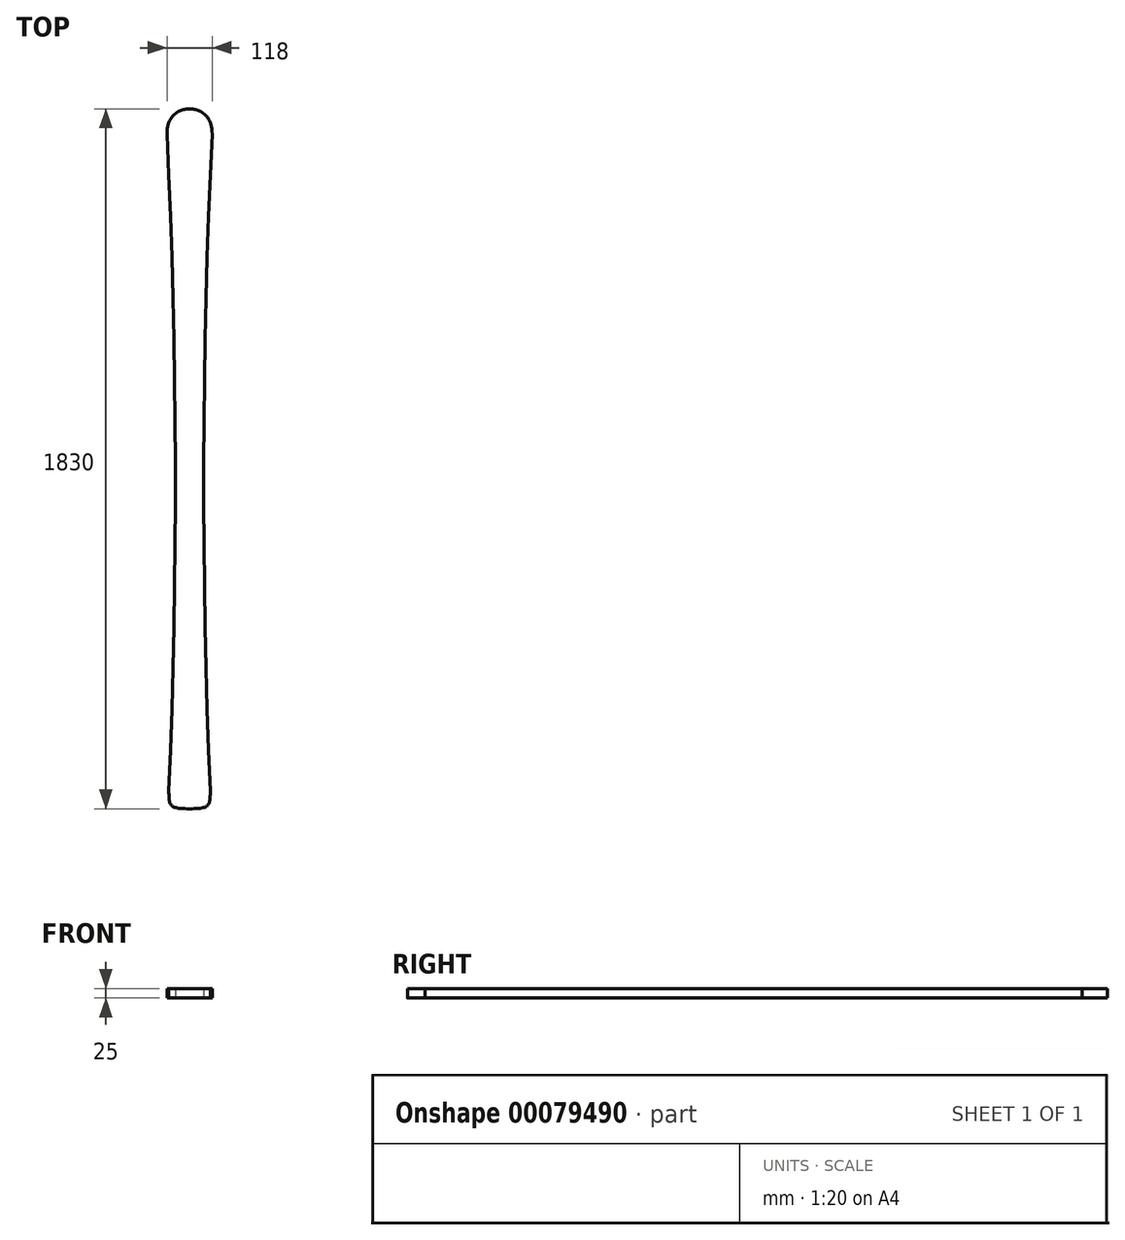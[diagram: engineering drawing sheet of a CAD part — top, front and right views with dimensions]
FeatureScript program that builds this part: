
annotation { "Feature Type Name" : "Feature", "Feature Type Description" : "" }
export const myFeature = defineFeature(function(context is Context, id is Id, definition is map)
    precondition{}
    {
        {
            var Q0;
            Q0=qCreatedBy(makeId("Top.planeOp"),FACE);
            var sketch = newSketch(context, id + "F0", { "sketchPlane" : qUnion([Q0])});
            skLineSegment(sketch, "E0", {"start": v(0, 0) * mm, "end": v(0, 1830) * mm, "construction": true});
            skLineSegment(sketch, "E1", {"start": v(0, 1830) * mm, "end": v(59, 1830) * mm, "construction": true});
            skLineSegment(sketch, "E2", {"start": v(59, 1830) * mm, "end": v(59, 0) * mm, "construction": true});
            skLineSegment(sketch, "E3", {"start": v(54, 0) * mm, "end": v(54, 46.44) * mm, "construction": true});
            skLineSegment(sketch, "E4", {"start": v(0, 1764.07) * mm, "end": v(59, 1764.07) * mm, "construction": true});
            skLineSegment(sketch, "E5", {"start": v(0, 46.44) * mm, "end": v(54, 46.44) * mm, "construction": true});
            skLineSegment(sketch, "E6", {"start": v(37, 1094.84) * mm, "end": v(37, 850) * mm, "construction": true});
            skArc(sketch, "E7", {"start": v(59, 1764.07) * mm, "mid": v(37.08, 905.3) * mm, "end": v(54, 46.44) * mm});
            skFitSpline(sketch, "E8", {"points": [v(59, 1764.07) * mm, v(0, 1830) * mm], "startDerivative": vector(0, 163.98) * mm, "endDerivative": vector(-63.63, 0) * mm});
            skFitSpline(sketch, "E9", {"points": [v(54, 46.44) * mm, v(0, 0) * mm], "startDerivative": vector(0, -114.92) * mm, "endDerivative": vector(-161.21, 0) * mm});
            skFitSpline(sketch, "E10.MirrorCS", {"points": [v(-59, 1764.07) * mm, v(0, 1830) * mm], "startDerivative": vector(0, 163.98) * mm, "endDerivative": vector(63.63, 0) * mm});
            skArc(sketch, "E11.MirrorCS", {"start": v(-59, 1764.07) * mm, "mid": v(-37.08, 905.3) * mm, "end": v(-54, 46.44) * mm});
            skFitSpline(sketch, "E12.MirrorCS", {"points": [v(-54, 46.44) * mm, v(0, 0) * mm], "startDerivative": vector(0, -114.92) * mm, "endDerivative": vector(161.21, 0) * mm});
            skPoint(sketch, "E13", {"position": v(37, 850) * mm});
            skSolve(sketch);
        }
        {
            var Q0;
            Q0=makeQuery(id+"F0.imprint","IMPRINT",FACE,{"disambiguationData":[TD([[makeQuery(id+"F0.imprint","IMPRINT",EDGE,{"derivedFrom":sQuery(id+"F0.wireOp",EDGE,"E7")}),-1.0]])]});
            extrude(context, id + "F1", {"entities" : qUnion([Q0]), "depth" : 25 * mm});
        }
    });
